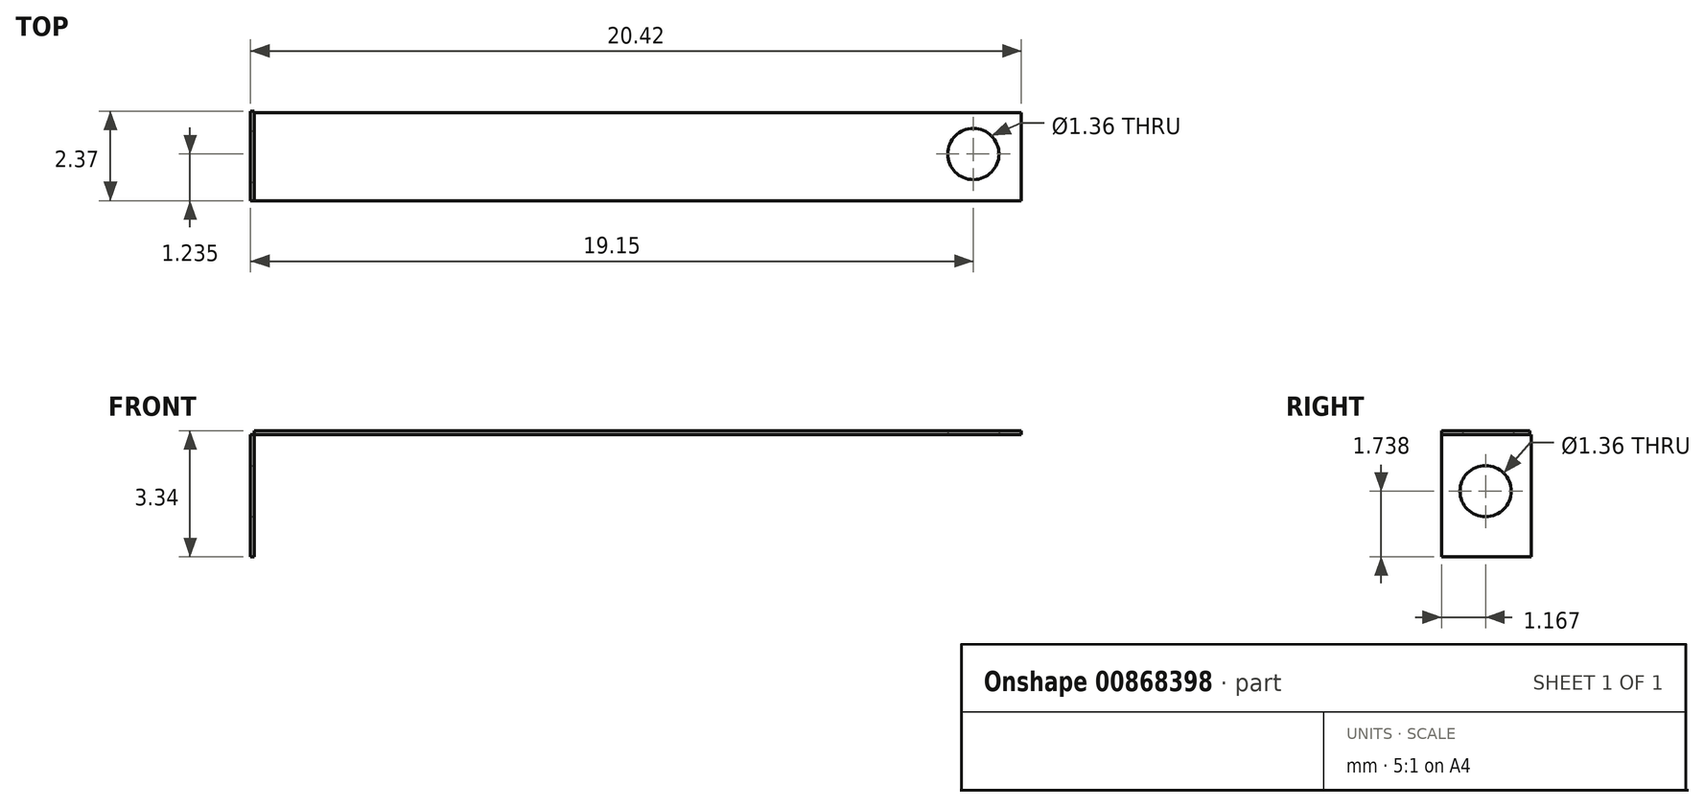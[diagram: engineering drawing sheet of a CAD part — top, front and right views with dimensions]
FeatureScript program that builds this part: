
annotation { "Feature Type Name" : "Feature", "Feature Type Description" : "" }
export const myFeature = defineFeature(function(context is Context, id is Id, definition is map)
    precondition{}
    {
        {
            var Q0;
            Q0=qCreatedBy(makeId("Top.planeOp"),FACE);
            var sketch = newSketch(context, id + "F0", { "sketchPlane" : qUnion([Q0])});
            skLineSegment(sketch, "E0.bottom", {"start": v(0, 0) * mm, "end": v(20.32, 0) * mm});
            skLineSegment(sketch, "E0.top", {"start": v(0, 2.34) * mm, "end": v(20.32, 2.34) * mm});
            skLineSegment(sketch, "E0.left", {"start": v(0, 0) * mm, "end": v(0, 2.34) * mm});
            skLineSegment(sketch, "E0.right", {"start": v(20.32, 0) * mm, "end": v(20.32, 2.34) * mm});
            skCircle(sketch, "E1", {"center": v(19.05, 1.24) * mm, "radius": 0.68 * mm});
            skLineSegment(sketch, "E2", {"start": v(19.05, 1.24) * mm, "end": v(0, 1.24) * mm});
            skSolve(sketch);
        }
        {
            var Q0;
            Q0=qCreatedBy(makeId("Right.planeOp"),FACE);
            var sketch = newSketch(context, id + "F1", { "sketchPlane" : qUnion([Q0])});
            skLineSegment(sketch, "E3.bottom", {"start": v(0, 0) * mm, "end": v(2.37, 0) * mm});
            skLineSegment(sketch, "E3.top", {"start": v(0, -3.24) * mm, "end": v(2.37, -3.24) * mm});
            skLineSegment(sketch, "E3.left", {"start": v(0, 0) * mm, "end": v(0, -3.24) * mm});
            skLineSegment(sketch, "E3.right", {"start": v(2.37, 0) * mm, "end": v(2.37, -3.24) * mm});
            skCircle(sketch, "E4", {"center": v(1.17, -1.5) * mm, "radius": 0.68 * mm});
            skSolve(sketch);
        }
        {
            var Q0;
            Q0=makeQuery(id+"F0.imprint","IMPRINT",FACE,{"disambiguationData":[TD([[makeQuery(id+"F0.imprint","IMPRINT",EDGE,{"derivedFrom":sQuery(id+"F0.wireOp",EDGE,"E0.bottom")}),1.0]])]});
            extrude(context, id + "F2", {"entities" : qUnion([Q0]), "depth" : 0.1 * mm, "offsetDistance" : 25.4 * mm});
        }
        {
            var Q0;
            Q0=makeQuery(id+"F1.imprint","IMPRINT",FACE,{"disambiguationData":[TD([[makeQuery(id+"F1.imprint","IMPRINT",EDGE,{"derivedFrom":sQuery(id+"F1.wireOp",EDGE,"E3.bottom")}),-1.0]])]});
            extrude(context, id + "F3", {"entities" : qUnion([Q0]), "operationType" : NewBodyOperationType.ADD, "oppositeDirection" : true, "depth" : 0.1 * mm, "offsetDistance" : 25.4 * mm});
        }
    });
